# Revit family: Bathroom_Accessory-Delta-Traditional_Decorative_ADA_Grab_Bar-24in
name_source: partatom
category: Plumbing Fixtures
revit_build: Autodesk Revit MEP 2014 (Build: 20140709_2115(x64)
units: mm (PartAtom-declared; Revit-internal decimal feet)

## types (5) — shared parameters
ADA Compliant = Yes
Actual Valve Water Flow = 0 GPM
CWC R = 0"
Cold Water Connection = 1"
Default Elevation = 3' - 9 1/4"
Finish = Chrome - DELTA - Polished
HWC R = 0"
Hot Water Connection = 1"
Manufacturer = DELTA
Product Documentation Link = http://www.deltafaucet.com
Product Page URL = https://www.deltafaucet.com
Series = Delta
URL = http://www.deltafaucet.com
Warranty URL = http://www.deltafaucet.com
zero-valued in all types: CWFU, Cost, HWFU, WFU

## per-type parameters (varying)
| type | Product Name | Width |
| 41624 | Traditional Decorative ADA Grab Bar - 24″ | 2' - 0" |
| 41618 | Traditional Decorative ADA Grab Bar - 18″ | 1' - 6" |
| 41612 | Traditional Decorative ADA Grab Bar - 12″ | 1' - 0" |
| 41636 | Traditional Decorative ADA Grab Bar - 36″ | 3' - 0" |
| 41642 | Traditional Decorative ADA Grab Bar - 42″ | 3' - 6" |

note: column(s) folded — value = type name in every type: Model

## geometry (parser evidence)
native form markers: Blend x12, Sweep x2
no freeform markers — native parametric forms only
